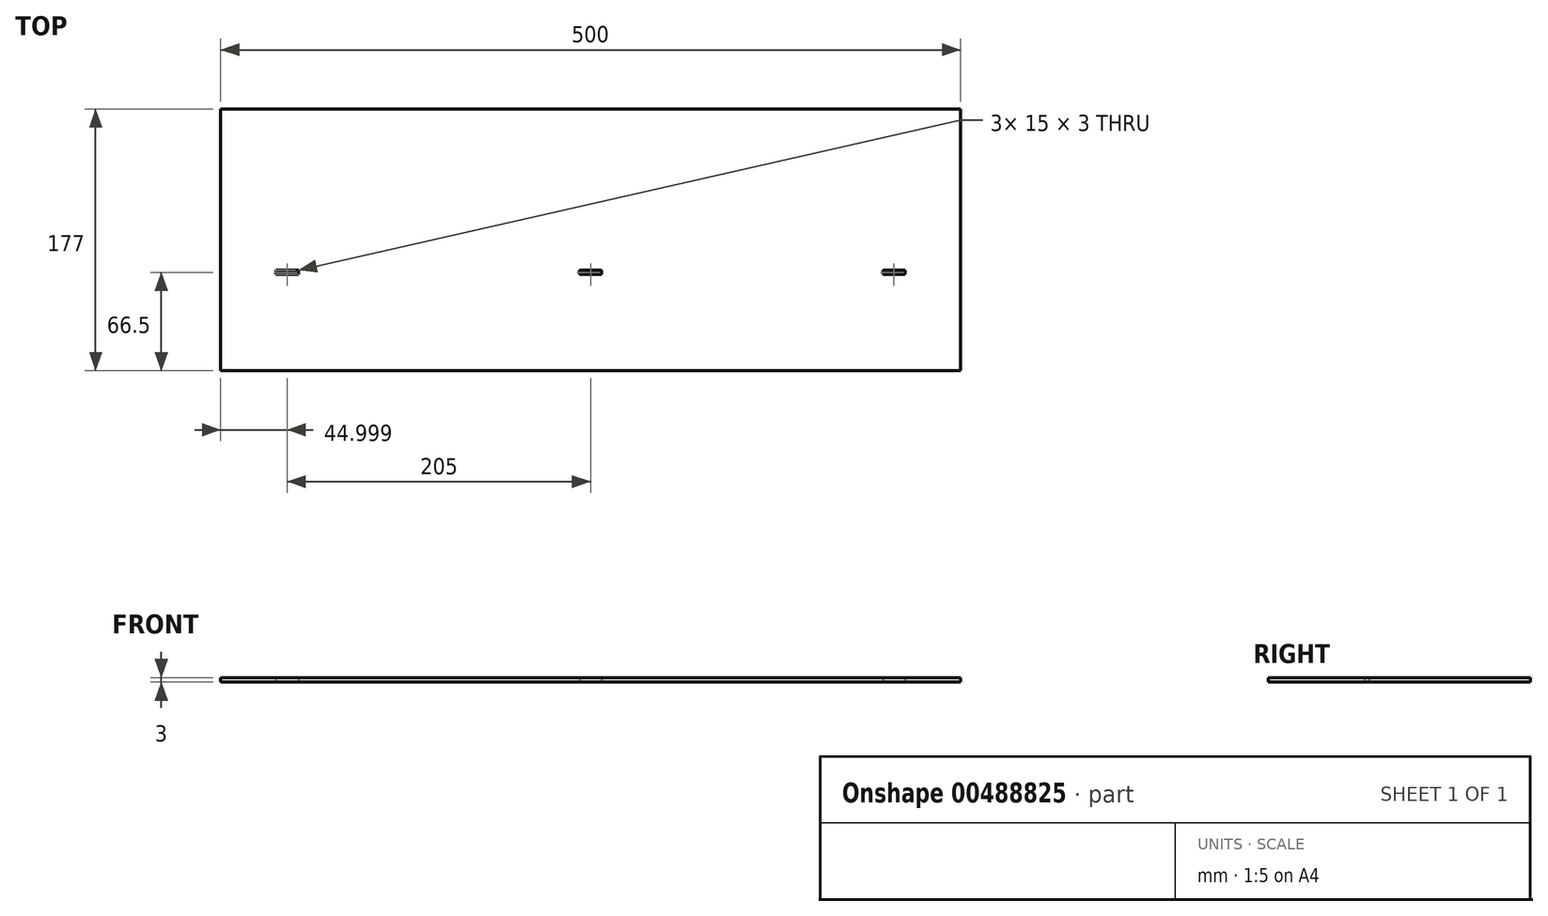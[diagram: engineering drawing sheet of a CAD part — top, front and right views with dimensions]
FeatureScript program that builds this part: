
annotation { "Feature Type Name" : "Feature", "Feature Type Description" : "" }
export const myFeature = defineFeature(function(context is Context, id is Id, definition is map)
    precondition{}
    {
        {
            var Q0;
            Q0=qCreatedBy(makeId("Top.planeOp"),FACE);
            var sketch = newSketch(context, id + "F0", { "sketchPlane" : qUnion([Q0])});
            skLineSegment(sketch, "E0.bottom", {"start": v(-252.74, 109) * mm, "end": v(247.26, 109) * mm});
            skLineSegment(sketch, "E0.top", {"start": v(-252.74, -68) * mm, "end": v(247.26, -68) * mm});
            skLineSegment(sketch, "E0.left", {"start": v(-252.74, 109) * mm, "end": v(-252.74, -68) * mm});
            skLineSegment(sketch, "E0.right", {"start": v(247.26, 109) * mm, "end": v(247.26, -68) * mm});
            skLineSegment(sketch, "E1.bottom", {"start": v(-215.24, 0) * mm, "end": v(-200.24, 0) * mm});
            skLineSegment(sketch, "E1.left", {"start": v(-215.24, 0) * mm, "end": v(-215.24, -3) * mm});
            skLineSegment(sketch, "E1.right", {"start": v(209.76, 0) * mm, "end": v(209.76, -3) * mm});
            skLineSegment(sketch, "E2.top", {"start": v(-215.24, -3) * mm, "end": v(-200.24, -3) * mm});
            skLineSegment(sketch, "E2.right", {"start": v(-200.24, 0) * mm, "end": v(-200.24, -3) * mm});
            skLineSegment(sketch, "E3.bottom", {"start": v(-10.24, 0) * mm, "end": v(4.76, 0) * mm});
            skLineSegment(sketch, "E3.top", {"start": v(-10.24, -3) * mm, "end": v(4.76, -3) * mm});
            skLineSegment(sketch, "E3.left", {"start": v(-10.24, 0) * mm, "end": v(-10.24, -3) * mm});
            skLineSegment(sketch, "E3.right", {"start": v(4.76, 0) * mm, "end": v(4.76, -3) * mm});
            skLineSegment(sketch, "E4.bottom", {"start": v(209.76, 0) * mm, "end": v(194.76, 0) * mm});
            skLineSegment(sketch, "E4.top", {"start": v(209.76, -3) * mm, "end": v(194.76, -3) * mm});
            skLineSegment(sketch, "E4.right", {"start": v(194.76, 0) * mm, "end": v(194.76, -3) * mm});
            skLineSegment(sketch, "E5.trimOffspring", {"start": v(194.76, 0) * mm, "end": v(209.76, 0) * mm});
            skLineSegment(sketch, "E6.trimOffspring", {"start": v(194.76, -3) * mm, "end": v(209.76, -3) * mm});
            skSolve(sketch);
        }
        {
            var Q0;
            Q0=makeQuery(id+"F0.imprint","IMPRINT",FACE,{"disambiguationData":[TD([[makeQuery(id+"F0.imprint","IMPRINT",EDGE,{"derivedFrom":sQuery(id+"F0.wireOp",EDGE,"E0.bottom")}),-1.0]])]});
            extrude(context, id + "F1", {"entities" : qUnion([Q0]), "depth" : 3 * mm});
        }
    });
